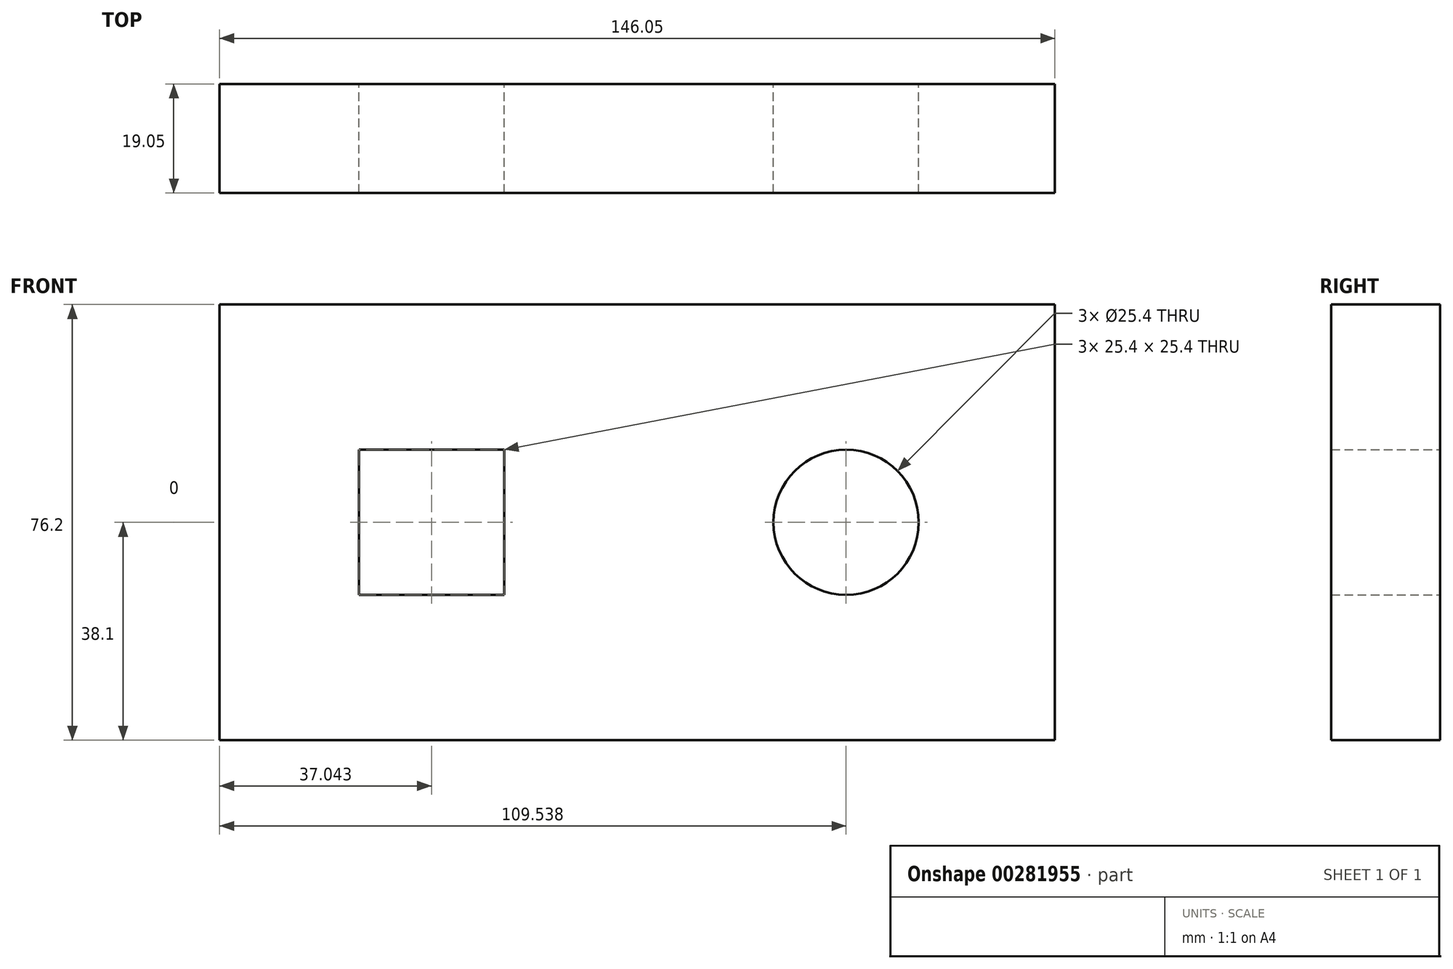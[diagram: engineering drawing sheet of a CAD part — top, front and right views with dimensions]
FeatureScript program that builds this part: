
annotation { "Feature Type Name" : "Feature", "Feature Type Description" : "" }
export const myFeature = defineFeature(function(context is Context, id is Id, definition is map)
    precondition{}
    {
        {
            var Q0;
            Q0=qCreatedBy(makeId("Front.planeOp"),FACE);
            var sketch = newSketch(context, id + "F0", { "sketchPlane" : qUnion([Q0])});
            skLineSegment(sketch, "E0.bottom", {"start": v(0, 0) * mm, "end": v(-146.05, 0) * mm});
            skLineSegment(sketch, "E0.top", {"start": v(0, 76.2) * mm, "end": v(-146.05, 76.2) * mm});
            skLineSegment(sketch, "E0.left", {"start": v(0, 0) * mm, "end": v(0, 76.2) * mm});
            skLineSegment(sketch, "E0.right", {"start": v(-146.05, 0) * mm, "end": v(-146.05, 76.2) * mm});
            skLineSegment(sketch, "E1.bottom", {"start": v(-96.3, 50.8) * mm, "end": v(-121.7, 50.8) * mm});
            skLineSegment(sketch, "E1.top", {"start": v(-96.3, 25.4) * mm, "end": v(-121.7, 25.4) * mm});
            skLineSegment(sketch, "E1.left", {"start": v(-96.3, 50.8) * mm, "end": v(-96.3, 25.4) * mm});
            skLineSegment(sketch, "E1.right", {"start": v(-121.7, 50.8) * mm, "end": v(-121.7, 25.4) * mm});
            skCircle(sketch, "E2", {"center": v(-36.51, 38.1) * mm, "radius": 12.7 * mm});
            skSolve(sketch);
        }
        {
            var Q0;
            Q0 = qSketchRegion(id + "F0", true);
            extrude(context, id + "F1", {"entities" : qUnion([Q0]), "depth" : 19.05 * mm});
        }
    });
